FCSTD DOCUMENT  (FreeCAD 0.20R29177 +426 (Git))
Label: BearingRotator
License: All rights reserved
LicenseURL: http://en.wikipedia.org/wiki/All_rights_reserved
objects: PartDesign::CoordinateSystem×2, Sketcher::SketchObject×1, PartDesign::Body×1
note: 4 computed .brp shape members not serialized (recipe doc carries the construction recipe); baked Part::Feature solids carry a one-line shape summary decoded from their .brp
EXTERNAL_REF file=assembly4.FCStd obj=Variables

FEATURE [Sketcher::SketchObject] Sketch  label="RotatorSketch"
  FullyConstrained = true
  MapMode = 5
  Support = -> [XY_Plane]
  expr: Constraints[2] = assembly4#Variables.BearingRotatorVar
  sketch-geometry (1):
    g0: LineSegment StartX=0 StartY=0 StartZ=0 EndX=-20 EndY=-34.641 EndZ=0
  constraints (3):
    c: Coincident(g0,g-1)
    c: Distance(g0) = 40
    c: Angle(g-1,g0) = -2.0944
FEATURE [PartDesign::CoordinateSystem] RotatorLCS
  AttacherType = Attacher::AttachEngine3D
  MapMode = 7
  Placement = pos=(0,0,0) rot=(0.186157,0.694747,0.694747;2.77349rad)
  Support = -> [Sketch]
FEATURE [PartDesign::CoordinateSystem] RotatorPosition
  AttacherType = Attacher::AttachEngine3D
FEATURE [PartDesign::Body] Body  label="RotatorBody"
  Group = -> [Sketch,RotatorLCS,RotatorPosition]
  Origin = -> Origin
